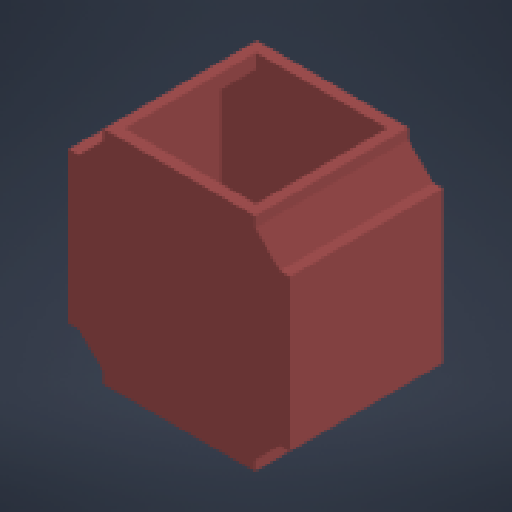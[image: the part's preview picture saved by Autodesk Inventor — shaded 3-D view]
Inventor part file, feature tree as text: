
AUTODESK INVENTOR PART (.ipt)
format: ipt  version: 2023.4 (Build 274418000, 418)  size: 181,248 bytes
history: native  units: mm
features: extrude x3, other x2, plane x1, reference x1, projected_geometry x1
ambient origin geometry x8: Origin, YZ Plane, XZ Plane, XY Plane, X Axis, Y Axis, Z Axis, Center Point
bodies: Solid1 (feature_tree)
feature tree (8):
  plane  "Work Plane1"
  extrude  "Extrusion1"  Depth=0.075mm
  extrude  "Extrusion2"  Depth=2.5mm TaperAngle=0.0deg
  extrude  "Extrusion3"  Depth=2.3mm
  reference  "Reference1"
  projected_geometry  "Projected Loop1"
  other  "Cube 1x1 V5.iam"
  other  "Cube 1x1 Bottom V5:1"
